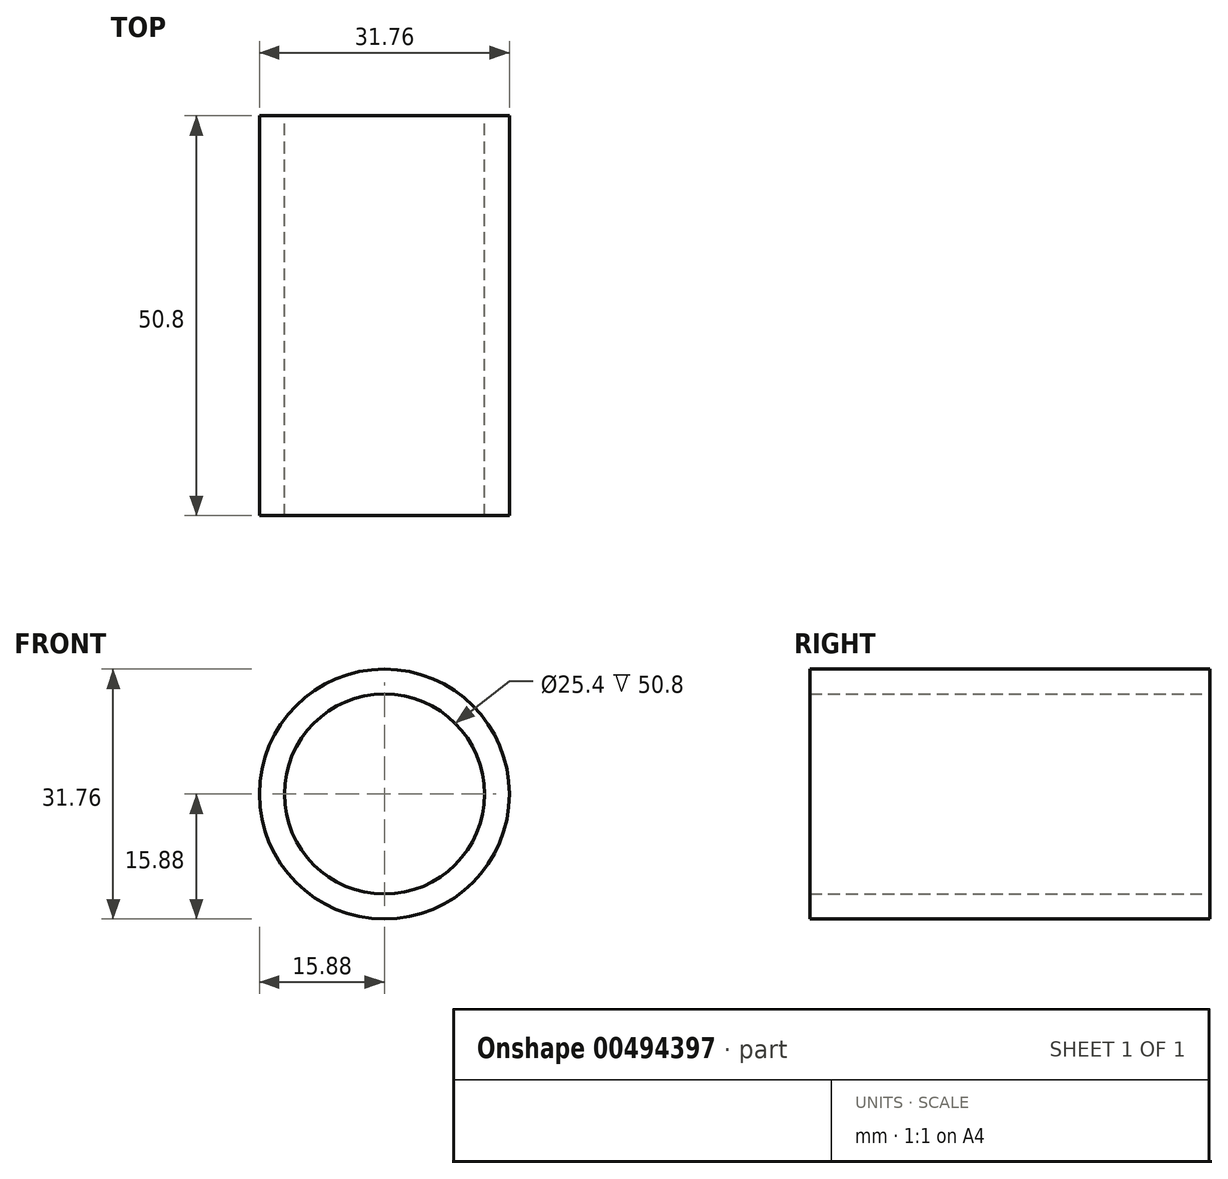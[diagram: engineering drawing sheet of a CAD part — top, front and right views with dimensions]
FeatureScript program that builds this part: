
annotation { "Feature Type Name" : "Feature", "Feature Type Description" : "" }
export const myFeature = defineFeature(function(context is Context, id is Id, definition is map)
    precondition{}
    {
        {
            var Q0;
            Q0=qCreatedBy(makeId("Front.planeOp"),FACE);
            var sketch = newSketch(context, id + "F0", { "sketchPlane" : qUnion([Q0])});
            skCircle(sketch, "E0", {"center": v(0, 0) * mm, "radius": 12.7 * mm});
            skCircle(sketch, "E1", {"center": v(0, 0) * mm, "radius": 15.88 * mm});
            skSolve(sketch);
        }
        {
            var Q0;
            Q0=makeQuery(id+"F0.imprint","IMPRINT",FACE,{"disambiguationData":[TD([[makeQuery(id+"F0.imprint","IMPRINT",EDGE,{"derivedFrom":sQuery(id+"F0.wireOp",EDGE,"E0")}),-1.0]])]});
            extrude(context, id + "F1", {"entities" : qUnion([Q0]), "depth" : 50.8 * mm});
        }
    });
